# Revit family: Faucet-Wall_Mount-Pot_Filler-KALLISTA-Juxtapose-P23181
name_source: partatom
category: Plumbing Fixtures
units: mm (PartAtom-declared; Revit-internal decimal feet)

## family parameters
Cut with Voids When Loaded = No
Host = Face
OmniClass Number = 23.31.11.00
OmniClass Title = Faucets
Part Type = Normal
Room Calculation Point = No
Round Connector Dimension = Use Diameter
Shared = No

## types (6) — shared parameters
ADA Compliant = No
Assembly Code = D2010
CW Connection = Yes
Cold Water Inlet = Cold Water Inlet
Date Modified = 11/16/2024
Default Elevation = 36"
Description = Wall-Mount Pot Filler
Drain Included = No
Flow Rate = 0 GPM
HW Connection = Yes
Handle Clearance = 2 11/16"
Height = 4 13/16"
Hot Water Inlet = Hot Water Inlet
L1 = 8 7/8"
L2 = 13 1/8"
Length = 22"
Manufacturer = Kallista Co.
Master Format 2014 = 22 41 39
Master Format 2014 Name = Residential Faucets, Supplies, and Trim
Material = Premium Metal Construction
Pressure = 0.00 psi
Product Documentation Link = https://resources.kohler.com
Product Name = Juxtapose
Spout Reach = 4 9/16"
URL = https://www.kallista.com
Vent Connection = No
Waste Connection = No
Waste Water Outlet = Waste Water Outlet
WaterSense Certified = No
Width = 2 3/4"

## per-type parameters (varying)
| type | Finish | Model | Product Page URL | Secondary Finish | Type |
| 00, BL-Matte Black | Kallista-Metal-BL-Matte_Black | P23181-00-BL | https://www.kallista.com | Kallista-Metal-BL-Matte_Black | 1 |
| 00, CP-Chrome | Kallista-Metal-CP-Chrome | P23181-00-CP | https://www.kallista.com | Kallista-Metal-CP-Chrome | 2 |
| 00, VS-Stainless | Kallista-Metal-VS-Stainless | P23181-00-VS | https://www.kallista.com | Kallista-Metal-VS-Stainless | 3 |
| 2MB, VS-Stainless | Kallista-Metal-VS-Stainless | P23181-2MB-VS |  | Kallista-Metal-2MB- Brushed_Brass | 4 |
| 2MB, BL-Matte Black | Kallista-Metal-BL-Matte_Black | P23181-2MB-BL | https://www.kallista.com | Kallista-Metal-2MB- Brushed_Brass | 5 |
| AF, BAF-Brushed French Gold | Kallista-Metal-BAF-Brushed_French_Gold | P23181-AF-BAF |  | Kallista-Metal-AF-French_Gold | 6 |

## geometry (parser evidence)
native form markers: Sweep x5
no freeform markers — native parametric forms only
